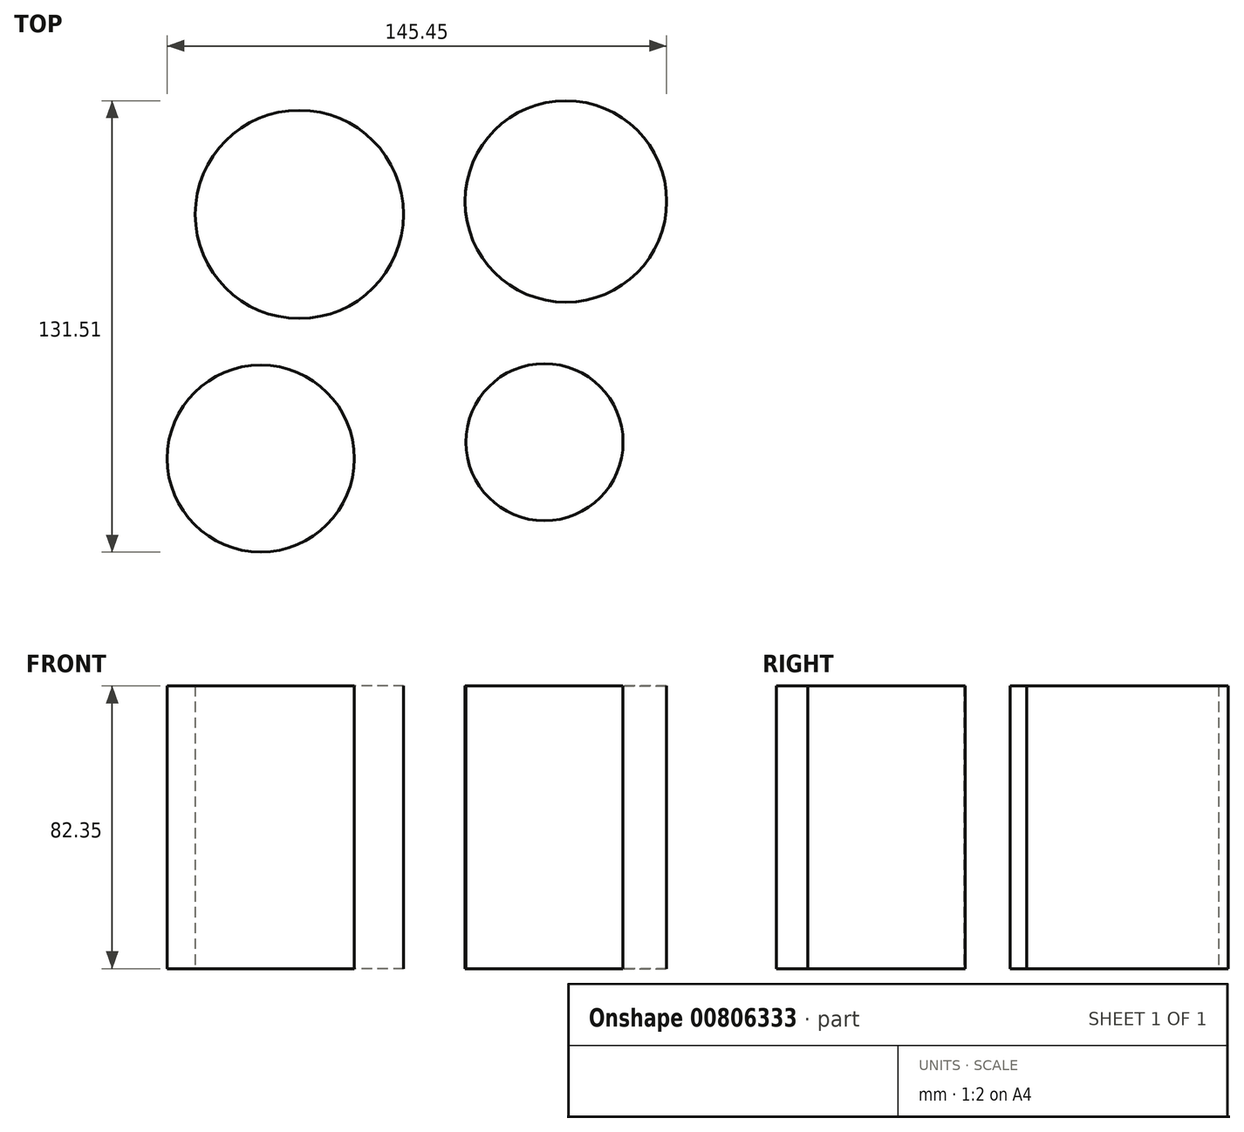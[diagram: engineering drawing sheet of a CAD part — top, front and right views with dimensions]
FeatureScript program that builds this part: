
annotation { "Feature Type Name" : "Feature", "Feature Type Description" : "" }
export const myFeature = defineFeature(function(context is Context, id is Id, definition is map)
    precondition{}
    {
        {
            var Q0;
            Q0=qCreatedBy(makeId("Top.planeOp"),FACE);
            var sketch = newSketch(context, id + "F0", { "sketchPlane" : qUnion([Q0])});
            skCircle(sketch, "E0", {"center": v(-39.23, 35.8) * mm, "radius": 30.34 * mm});
            skCircle(sketch, "E1", {"center": v(38.37, 39.6) * mm, "radius": 29.35 * mm});
            skCircle(sketch, "E2", {"center": v(-50.47, -35.32) * mm, "radius": 27.26 * mm});
            skCircle(sketch, "E3", {"center": v(32.14, -30.55) * mm, "radius": 22.9 * mm});
            skSolve(sketch);
        }
        {
            var Q0;
            Q0=makeQuery(id+"F0.imprint","IMPRINT",FACE,{"disambiguationData":[TD([[makeQuery(id+"F0.imprint","IMPRINT",EDGE,{"derivedFrom":sQuery(id+"F0.wireOp",EDGE,"E0")}),1.0]])]});
            var Q1;
            Q1=makeQuery(id+"F0.imprint","IMPRINT",FACE,{"disambiguationData":[TD([[makeQuery(id+"F0.imprint","IMPRINT",EDGE,{"derivedFrom":sQuery(id+"F0.wireOp",EDGE,"E1")}),1.0]])]});
            var Q2;
            Q2=makeQuery(id+"F0.imprint","IMPRINT",FACE,{"disambiguationData":[TD([[makeQuery(id+"F0.imprint","IMPRINT",EDGE,{"derivedFrom":sQuery(id+"F0.wireOp",EDGE,"E3")}),1.0]])]});
            var Q3;
            Q3=makeQuery(id+"F0.imprint","IMPRINT",FACE,{"disambiguationData":[TD([[makeQuery(id+"F0.imprint","IMPRINT",EDGE,{"derivedFrom":sQuery(id+"F0.wireOp",EDGE,"E2")}),1.0]])]});
            extrude(context, id + "F1", {"entities" : qUnion([Q0, Q1, Q2, Q3]), "depth" : 82.35 * mm, "offsetDistance" : 25.4 * mm});
        }
    });
